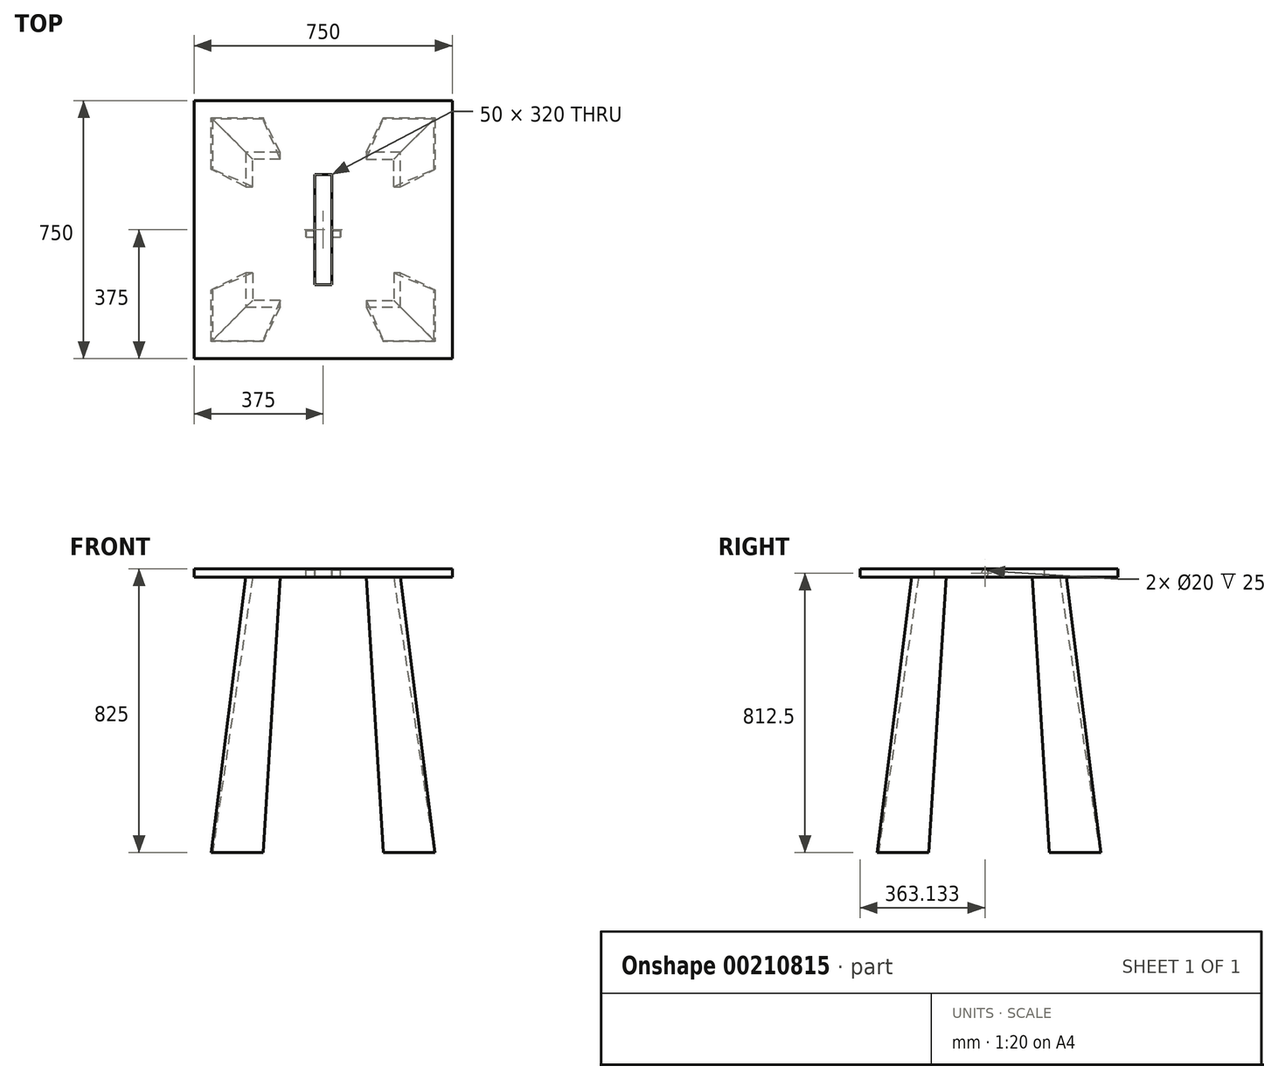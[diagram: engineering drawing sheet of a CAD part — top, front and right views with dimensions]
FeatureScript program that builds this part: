
annotation { "Feature Type Name" : "Feature", "Feature Type Description" : "" }
export const myFeature = defineFeature(function(context is Context, id is Id, definition is map)
    precondition{}
    {
        {
            assignVariable(context, id + "F0", {"variableType" : VariableType.LENGTH, "name" : "ALTO_MESA", "lengthValue" : 800 * mm});
        }
        {
            var Q0;
            Q0=qCreatedBy(makeId("Top.planeOp"),FACE);
            var sketch = newSketch(context, id + "F1", { "sketchPlane" : qUnion([Q0])});
            skLineSegment(sketch, "E0", {"start": v(-325, 175) * mm, "end": v(-322, 175) * mm});
            skLineSegment(sketch, "E1", {"start": v(-325, 175) * mm, "end": v(-325, 325) * mm});
            skLineSegment(sketch, "E2", {"start": v(-325, 325) * mm, "end": v(-175, 325) * mm});
            skLineSegment(sketch, "E3", {"start": v(-175, 325) * mm, "end": v(-175, 322) * mm});
            skLineSegment(sketch, "E4", {"start": v(-175, 322) * mm, "end": v(-322, 322) * mm});
            skLineSegment(sketch, "E5", {"start": v(-322, 322) * mm, "end": v(-322, 175) * mm});
            skPoint(sketch, "E6", {"position": v(-322, 322) * mm});
            skPoint(sketch, "E7.1.0", {"position": v(-322, -322) * mm});
            skLineSegment(sketch, "E7.1.1", {"start": v(-322, -175) * mm, "end": v(-322, -322) * mm});
            skLineSegment(sketch, "E7.1.2", {"start": v(-325, -325) * mm, "end": v(-325, -175) * mm});
            skLineSegment(sketch, "E7.1.3", {"start": v(-175, -325) * mm, "end": v(-325, -325) * mm});
            skLineSegment(sketch, "E7.1.4", {"start": v(-322, -322) * mm, "end": v(-175, -322) * mm});
            skLineSegment(sketch, "E7.1.5", {"start": v(-175, -325) * mm, "end": v(-175, -322) * mm});
            skLineSegment(sketch, "E7.1.6", {"start": v(-325, -175) * mm, "end": v(-322, -175) * mm});
            skPoint(sketch, "E7.2.0", {"position": v(322, -322) * mm});
            skLineSegment(sketch, "E7.2.1", {"start": v(175, -322) * mm, "end": v(322, -322) * mm});
            skLineSegment(sketch, "E7.2.2", {"start": v(325, -325) * mm, "end": v(175, -325) * mm});
            skLineSegment(sketch, "E7.2.3", {"start": v(325, -175) * mm, "end": v(325, -325) * mm});
            skLineSegment(sketch, "E7.2.4", {"start": v(322, -322) * mm, "end": v(322, -175) * mm});
            skLineSegment(sketch, "E7.2.5", {"start": v(325, -175) * mm, "end": v(322, -175) * mm});
            skLineSegment(sketch, "E7.2.6", {"start": v(175, -325) * mm, "end": v(175, -322) * mm});
            skPoint(sketch, "E7.3.0", {"position": v(322, 322) * mm});
            skLineSegment(sketch, "E7.3.1", {"start": v(322, 175) * mm, "end": v(322, 322) * mm});
            skLineSegment(sketch, "E7.3.2", {"start": v(325, 325) * mm, "end": v(325, 175) * mm});
            skLineSegment(sketch, "E7.3.3", {"start": v(175, 325) * mm, "end": v(325, 325) * mm});
            skLineSegment(sketch, "E7.3.4", {"start": v(322, 322) * mm, "end": v(175, 322) * mm});
            skLineSegment(sketch, "E7.3.5", {"start": v(175, 325) * mm, "end": v(175, 322) * mm});
            skLineSegment(sketch, "E7.3.6", {"start": v(325, 175) * mm, "end": v(322, 175) * mm});
            skPoint(sketch, "E7.center", {"position": v(0, 0) * mm});
            skLineSegment(sketch, "E8", {"start": v(-322, 175) * mm, "end": v(-322, -175) * mm, "construction": true});
            skCircle(sketch, "E9", {"center": v(0, 0) * mm, "radius": 15 * mm});
            skSolve(sketch);
        }
        {
            var Q0;
            Q0=qCreatedBy(makeId("Top.planeOp"),FACE);
            cPlane(context, id + "F2", {"entities" : qUnion([Q0]), "cplaneType" : CPlaneType.OFFSET, "offset" : getVariable(context, 'ALTO_MESA'), "width" : 150 * mm, "height" : 150 * mm});
        }
        {
            var Q0;
            Q0=qCreatedBy(id+"F2.planeOp",FACE);
            var sketch = newSketch(context, id + "F3", { "sketchPlane" : qUnion([Q0])});
            skLineSegment(sketch, "E10.bottom", {"start": v(225, 225) * mm, "end": v(-225, 225) * mm});
            skLineSegment(sketch, "E10.top", {"start": v(225, -225) * mm, "end": v(-225, -225) * mm});
            skLineSegment(sketch, "E10.left", {"start": v(225, 225) * mm, "end": v(225, -225) * mm});
            skLineSegment(sketch, "E10.right", {"start": v(-225, 225) * mm, "end": v(-225, -225) * mm});
            skPoint(sketch, "E10.middle", {"position": v(0, 0) * mm});
            skLineSegment(sketch, "E11.bottom", {"start": v(-225, 125) * mm, "end": v(-125, 125) * mm});
            skLineSegment(sketch, "E11.top", {"start": v(-225, 225) * mm, "end": v(-125, 225) * mm});
            skLineSegment(sketch, "E11.left", {"start": v(-225, 125) * mm, "end": v(-225, 225) * mm});
            skLineSegment(sketch, "E11.right", {"start": v(-125, 125) * mm, "end": v(-125, 225) * mm});
            skLineSegment(sketch, "E12.bottom", {"start": v(-125, 125) * mm, "end": v(-205, 125) * mm});
            skLineSegment(sketch, "E12.top", {"start": v(-125, 205) * mm, "end": v(-205, 205) * mm});
            skLineSegment(sketch, "E12.left", {"start": v(-125, 125) * mm, "end": v(-125, 205) * mm});
            skLineSegment(sketch, "E12.right", {"start": v(-205, 125) * mm, "end": v(-205, 205) * mm});
            skLineSegment(sketch, "E13.0", {"start": v(375, 375) * mm, "end": v(-375, 375) * mm});
            skLineSegment(sketch, "E13.1", {"start": v(375, 375) * mm, "end": v(375, -375) * mm});
            skLineSegment(sketch, "E13.2", {"start": v(375, -375) * mm, "end": v(-375, -375) * mm});
            skLineSegment(sketch, "E13.3", {"start": v(-375, 375) * mm, "end": v(-375, -375) * mm});
            skLineSegment(sketch, "E14.bottom", {"start": v(25, 160) * mm, "end": v(-25, 160) * mm});
            skLineSegment(sketch, "E14.top", {"start": v(25, -160) * mm, "end": v(-25, -160) * mm});
            skLineSegment(sketch, "E14.left", {"start": v(25, 160) * mm, "end": v(25, -160) * mm});
            skLineSegment(sketch, "E14.right", {"start": v(-25, 160) * mm, "end": v(-25, -160) * mm});
            skSolve(sketch);
        }
        {
            var Q0;
            {var subQ8=sQuery(id+"F3.wireOp",EDGE,"E12.top");Q0=makeQuery(id+"F3.imprint","IMPRINT",FACE,{"disambiguationData":[TD([[makeQuery(id+"F3.imprint","IMPRINT",EDGE,{"derivedFrom":subQ8}),-1.0]])]});}
            var Q1;
            Q1=makeQuery(id+"F1.imprint","IMPRINT",FACE,{"disambiguationData":[TD([[makeQuery(id+"F1.imprint","IMPRINT",EDGE,{"derivedFrom":sQuery(id+"F1.wireOp",EDGE,"E0")}),1.0]])]});
            var Q2;
            Q2=sQuery(id+"F3.wireOp",EDGE,"E10.left");
            var Q3;
            {var subQ8=sQuery(id+"F3.wireOp",EDGE,"E12.top");Q3=makeQuery(id+"F3.imprint","IMPRINT",FACE,{"disambiguationData":[TD([[makeQuery(id+"F3.imprint","IMPRINT",EDGE,{"derivedFrom":subQ8}),-1.0]])]});}
            var Q4;
            Q4=makeQuery(id+"F1.imprint","IMPRINT",FACE,{"disambiguationData":[TD([[makeQuery(id+"F1.imprint","IMPRINT",EDGE,{"derivedFrom":sQuery(id+"F1.wireOp",EDGE,"E0")}),1.0]])]});
            loft(context, id + "F4", {"sheetProfilesArray" : [{ "sheetProfileEntities" : qUnion([Q0]) }, { "sheetProfileEntities" : qUnion([Q1]) }], "wireProfilesArray" : [{ "wireProfileEntities" : qUnion([Q2]) }, { "wireProfileEntities" : qUnion([Q3]) }, { "wireProfileEntities" : qUnion([Q4]) }]});
        }
        {
            var Q0;
            {var subQ8=sQuery(id+"F3.wireOp",EDGE,"E12.top");Q0=makeQuery(id+"F4.opLoft","SWEPT_BODY",BODY,{"disambiguationData":[OSD([makeQuery(id+"F1.imprint","IMPRINT",FACE,{"disambiguationData":[TD([[makeQuery(id+"F1.imprint","IMPRINT",EDGE,{"derivedFrom":sQuery(id+"F1.wireOp",EDGE,"E0")}),1.0]])]}),makeQuery(id+"F3.imprint","IMPRINT",FACE,{"disambiguationData":[TD([[makeQuery(id+"F3.imprint","IMPRINT",EDGE,{"derivedFrom":subQ8}),-1.0]])]})])]});}
            var Q1;
            Q1=sQuery(id+"F1.wireOp",EDGE,"E9");
            circularPattern(context, id + "F5", {"entities" : qUnion([Q0]), "axis" : qUnion([Q1]), "angle" : 360 * degree, "instanceCount" : 4, "equalSpace" : true});
        }
        {
            var Q0;
            {var subQ1=sQuery(id+"F3.wireOp",EDGE,"E10.top");Q0=makeQuery(id+"F3.imprint","IMPRINT",FACE,{"disambiguationData":[TD([[makeQuery(id+"F3.imprint","IMPRINT",EDGE,{"derivedFrom":subQ1}),1.0]])]});}
            var Q1;
            {var subQ1=sQuery(id+"F3.wireOp",EDGE,"E10.top");Q1=makeQuery(id+"F3.imprint","IMPRINT",FACE,{"disambiguationData":[TD([[makeQuery(id+"F3.imprint","IMPRINT",EDGE,{"derivedFrom":subQ1}),-1.0]])]});}
            var Q2;
            {var subQ4=sQuery(id+"F3.wireOp",EDGE,"E12.top");Q2=makeQuery(id+"F3.imprint","IMPRINT",FACE,{"disambiguationData":[TD([[makeQuery(id+"F3.imprint","IMPRINT",EDGE,{"derivedFrom":subQ4}),1.0]])]});}
            var Q3;
            {var subQ3=sQuery(id+"F3.wireOp",EDGE,"E12.top");Q3=makeQuery(id+"F3.imprint","IMPRINT",FACE,{"disambiguationData":[TD([[makeQuery(id+"F3.imprint","IMPRINT",EDGE,{"derivedFrom":subQ3}),-1.0]])]});}
            extrude(context, id + "F6", {"entities" : qUnion([Q0, Q1, Q2, Q3]), "depth" : 25 * mm, "offsetDistance" : 25 * mm});
        }
        {
            var Q0;
            Q0=makeQuery(id+"F6.opExtrude","SWEPT_FACE",FACE,{"disambiguationData":[OSD([sQuery(id+"F3.wireOp",EDGE,"E14.right")])]});
            var sketch = newSketch(context, id + "F7", { "sketchPlane" : qUnion([Q0])});
            skCircle(sketch, "E15", {"center": v(-11.87, 812.5) * mm, "radius": 10 * mm});
            skPoint(sketch, "E15.centerSnap0", {"position": v(-160, 812.5) * mm});
            skSolve(sketch);
        }
        {
            var Q0;
            Q0=makeQuery(id+"F7.imprint","IMPRINT",FACE,{"disambiguationData":[TD([[makeQuery(id+"F7.imprint","IMPRINT",EDGE,{"derivedFrom":sQuery(id+"F7.wireOp",EDGE,"E15")}),1.0]])]});
            var Q1;
            Q1=makeQuery(id+"F6.opExtrude","SWEPT_FACE",FACE,{"disambiguationData":[OSD([sQuery(id+"F3.wireOp",EDGE,"E14.left")])]});
            extrude(context, id + "F8", {"entities" : qUnion([Q0]), "operationType" : NewBodyOperationType.REMOVE, "oppositeDirection" : true, "depth" : 25 * mm, "offsetDistance" : 25 * mm, "hasSecondDirection" : true, "secondDirectionBound" : SecondDirectionBoundingType.UP_TO_SURFACE, "secondDirectionOppositeDirection" : false, "secondDirectionDepth" : 25 * mm, "secondDirectionBoundEntityFace" : qUnion([Q1]), "hasSecondDirectionOffset" : true, "secondDirectionOffsetDistance" : 25 * mm, "secondDirectionOffsetOppositeDirection" : true});
        }
    });
